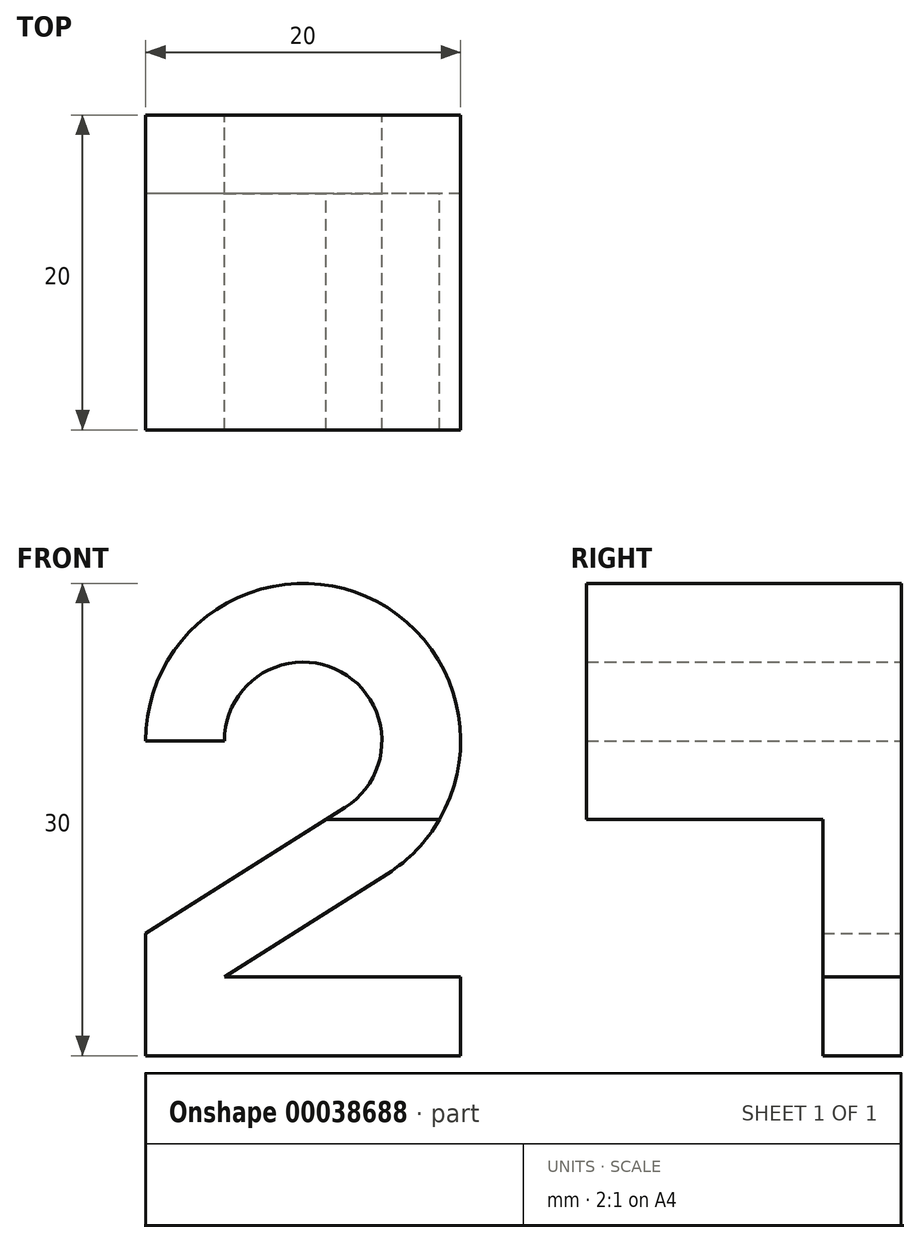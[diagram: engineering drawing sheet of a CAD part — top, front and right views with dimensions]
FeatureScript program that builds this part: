
annotation { "Feature Type Name" : "Feature", "Feature Type Description" : "" }
export const myFeature = defineFeature(function(context is Context, id is Id, definition is map)
    precondition{}
    {
        {
            var Q0;
            Q0=qCreatedBy(makeId("Front.planeOp"),FACE);
            var sketch = newSketch(context, id + "F0", { "sketchPlane" : qUnion([Q0])});
            skLineSegment(sketch, "E0", {"start": v(0, 0) * mm, "end": v(0, 7.75) * mm});
            skLineSegment(sketch, "E1", {"start": v(0, 7.75) * mm, "end": v(12.67, 15.78) * mm});
            skArc(sketch, "E2", {"start": v(12.67, 15.78) * mm, "mid": v(12.41, 24.38) * mm, "end": v(5, 20) * mm});
            skLineSegment(sketch, "E3", {"start": v(5, 20) * mm, "end": v(0, 20) * mm});
            skArc(sketch, "E4", {"start": v(15.35, 11.55) * mm, "mid": v(14.82, 28.76) * mm, "end": v(0, 20) * mm});
            skLineSegment(sketch, "E5", {"start": v(15.35, 11.55) * mm, "end": v(5, 5) * mm});
            skLineSegment(sketch, "E6", {"start": v(5, 5) * mm, "end": v(20, 5) * mm});
            skLineSegment(sketch, "E7", {"start": v(20, 5) * mm, "end": v(20, 0) * mm});
            skLineSegment(sketch, "E8", {"start": v(20, 0) * mm, "end": v(0, 0) * mm});
            skLineSegment(sketch, "E9", {"start": v(0, 30) * mm, "end": v(20, 30) * mm, "construction": true});
            skSolve(sketch);
        }
        {
            var Q0;
            Q0 = qSketchRegion(id + "F0", true);
            extrude(context, id + "F1", {"entities" : qUnion([Q0]), "depth" : 20 * mm});
        }
        {
            var Q0;
            Q0=qCreatedBy(makeId("Right.planeOp"),FACE);
            var sketch = newSketch(context, id + "F2", { "sketchPlane" : qUnion([Q0])});
            skLineSegment(sketch, "E10.bottom", {"start": v(0, 0) * mm, "end": v(-20, 0) * mm});
            skLineSegment(sketch, "E10.top", {"start": v(0, 30) * mm, "end": v(-20, 30) * mm});
            skLineSegment(sketch, "E10.left", {"start": v(0, 0) * mm, "end": v(0, 30) * mm});
            skLineSegment(sketch, "E10.right", {"start": v(-20, 0) * mm, "end": v(-20, 30) * mm});
            skLineSegment(sketch, "E11.bottom", {"start": v(-15, 30) * mm, "end": v(-5, 30) * mm});
            skLineSegment(sketch, "E11.top", {"start": v(-15, 20) * mm, "end": v(-5, 20) * mm});
            skLineSegment(sketch, "E11.left", {"start": v(-15, 30) * mm, "end": v(-15, 20) * mm});
            skLineSegment(sketch, "E11.right", {"start": v(-5, 30) * mm, "end": v(-5, 20) * mm});
            skLineSegment(sketch, "E12.bottom", {"start": v(-20, 15) * mm, "end": v(-5, 15) * mm});
            skLineSegment(sketch, "E12.top", {"start": v(-20, 0) * mm, "end": v(-5, 0) * mm});
            skLineSegment(sketch, "E12.left", {"start": v(-20, 15) * mm, "end": v(-20, 0) * mm});
            skLineSegment(sketch, "E12.right", {"start": v(-5, 15) * mm, "end": v(-5, 0) * mm});
            skSolve(sketch);
        }
        {
            var Q0;
            Q0=makeQuery(id+"F2.imprint","IMPRINT",FACE,{"disambiguationData":[TD([[makeQuery(id+"F2.imprint","IMPRINT",EDGE,{"derivedFrom":sQuery(id+"F2.wireOp",EDGE,"E11.bottom")}),-1.0]])]});
            var Q1;
            Q1=makeQuery(id+"F2.imprint","IMPRINT",FACE,{"disambiguationData":[TD([[makeQuery(id+"F2.imprint","IMPRINT",EDGE,{"derivedFrom":sQuery(id+"F2.wireOp",EDGE,"E12.bottom")}),-1.0]])]});
            extrude(context, id + "F3", {"entities" : qUnion([Q0, Q1]), "operationType" : NewBodyOperationType.REMOVE, "endBound" : BoundingType.SYMMETRIC, "depth" : 113.56 * mm});
        }
    });
